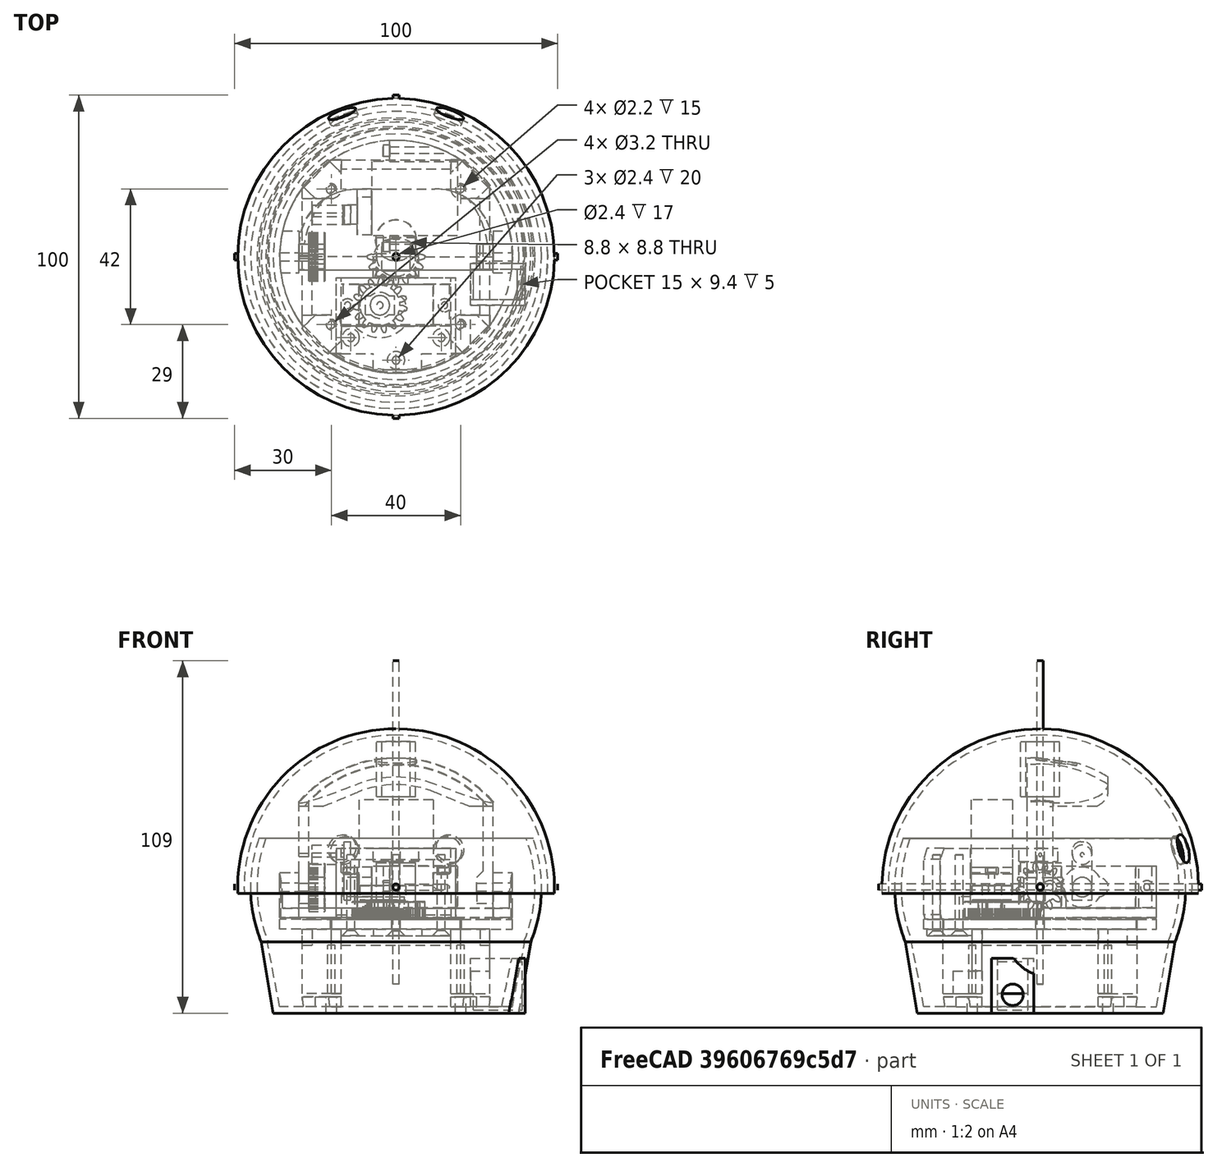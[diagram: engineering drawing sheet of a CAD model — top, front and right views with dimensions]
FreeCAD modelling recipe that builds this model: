
FCSTD DOCUMENT  (FreeCAD 0.18R16146 (Git))
Label: 2AxisDrive
License: All rights reserved
LicenseURL: http://en.wikipedia.org/wiki/All_rights_reserved
objects: Part::Cylinder×41, Part::Box×40, Part::Cut×20, Part::MultiFuse×20, Part::Chamfer×17, Part::Fillet×15, Part::Sphere×7, Part::Feature×4, Part::FeaturePython×3, Part::MultiCommon×3, Part::Cone×2
note: 172 computed .brp shape members not serialized (recipe doc carries the construction recipe); baked Part::Feature solids carry a one-line shape summary decoded from their .brp

FEATURE [Part::Cylinder] Cylinder001  label="Axis_Z"
  Angle = 360
  AttacherType = Attacher::AttachEngine3D
  Height = 100
  Placement = pos=(0,0,-30) rot=(0,0,1;0rad)
  Radius = 1
FEATURE [Part::Cylinder] Cylinder002  label="Axis_Y"
  Angle = 360
  AttacherType = Attacher::AttachEngine3D
  Height = 100
  Placement = pos=(0,50,0) rot=(1,0,0;1.5708rad)
  Radius = 1
FEATURE [Part::Cylinder] Cylinder003  label="Axis_X"
  Angle = 360
  AttacherType = Attacher::AttachEngine3D
  Height = 100
  Placement = pos=(-50,0,0) rot=(0,1,0;1.5708rad)
  Radius = 1
FEATURE [Part::Feature] Fusion001003001001006003002002001  label="Servo_1"
  Placement = pos=(-5,-15,3) rot=(0,0,1;1.5708rad)
  shape: bbox 33 x 12.8 x 35.5 mm, 23 faces (baked)
FEATURE [Part::Cone] Cone
  Angle = 360
  AttacherType = Attacher::AttachEngine3D
  Height = 21
  Placement = pos=(0,0,-37) rot=(0,0,1;0rad)
  Radius1 = 36
  Radius2 = 40
FEATURE [Part::Cone] Cone001
  Angle = 360
  AttacherType = Attacher::AttachEngine3D
  Height = 22.1
  Placement = pos=(0,0,-39) rot=(0,0,1;0rad)
  Radius1 = 38
  Radius2 = 41.7
FEATURE [Part::Sphere] Sphere001
  Angle1 = -90
  Angle2 = 90
  Angle3 = 360
  AttacherType = Attacher::AttachEngine3D
  Radius = 43
FEATURE [Part::Sphere] Sphere002
  Angle1 = -90
  Angle2 = 90
  Angle3 = 360
  AttacherType = Attacher::AttachEngine3D
  Radius = 45
FEATURE [Part::Box] Box027  label="Limit002"
  AttacherType = Attacher::AttachEngine3D
  Height = 50
  Length = 120
  Placement = pos=(-60,-60,15) rot=(0,0,1;0rad)
  Width = 120
FEATURE [Part::Cut] Cut007
  Base = -> Sphere002
  Tool = -> Sphere001
FEATURE [Part::Box] Box028  label="Limit003"
  AttacherType = Attacher::AttachEngine3D
  Height = 50
  Length = 120
  Placement = pos=(-60,-60,-67) rot=(0,0,1;0rad)
  Width = 120
FEATURE [Part::MultiFuse] Fusion001003001001006003002002007  label="BoxLimiters"
  Shapes = -> [Box028,Box027]
FEATURE [Part::Cut] Cut008  label="BoxRadius"
  Base = -> Cut007
  Tool = -> Fusion001003001001006003002002007
FEATURE [Part::Sphere] Sphere003
  Angle1 = -90
  Angle2 = 90
  Angle3 = 360
  AttacherType = Attacher::AttachEngine3D
  Radius = 49
FEATURE [Part::Sphere] Sphere004
  Angle1 = -90
  Angle2 = 90
  Angle3 = 360
  AttacherType = Attacher::AttachEngine3D
  Radius = 47
FEATURE [Part::Box] Box029  label="Limit004"
  AttacherType = Attacher::AttachEngine3D
  Height = 65
  Length = 120
  Placement = pos=(-60,-60,-67) rot=(0,0,1;0rad)
  Width = 120
FEATURE [Part::Cut] Cut010
  Base = -> Sphere003
  Tool = -> Sphere004
FEATURE [Part::Cut] Cut011  label="BoxTop"
  Base = -> Cut010
  Tool = -> Box029
FEATURE [Part::Box] Box030  label="Cube023"
  AttacherType = Attacher::AttachEngine3D
  Height = 17
  Length = 12
  Placement = pos=(-6,-6,28) rot=(0,0,1;0rad)
  Width = 12
FEATURE [Part::Box] Box031  label="Cube024"
  AttacherType = Attacher::AttachEngine3D
  Height = 20
  Length = 8.8
  Placement = pos=(-4.4,-4.4,28) rot=(0,0,1;0rad)
  Width = 8.8
FEATURE [Part::Cut] Cut012
  Base = -> Box030
  Tool = -> Box031
FEATURE [Part::MultiFuse] Fusion001003001001006003002002009  label="BoxCover"
  Shapes = -> [Cut012,Cut011]
FEATURE [Part::Feature] Fusion001003001001006003002002015001  label="EyeHolles"
  Placement = pos=(0,0,0) rot=(1,0,0;0.261799rad)
  shape: bbox 49.5 x 58.24 x 23.32 mm, 6 faces (baked)
FEATURE [Part::Feature] Fusion001003001001006003002002015002001  label="Fusion001003001001006003002002015003"
  Placement = pos=(0,0,0) rot=(1,0,0;0.261799rad)
  shape: bbox 40.43 x 44.55 x 21.37 mm, 6 faces (baked)
FEATURE [Part::MultiFuse] Fusion001003001001006003002002015002002
  Shapes = -> [Fusion001003001001006003002002015002001,Fusion001003001001006003002002015001]
FEATURE [Part::Cut] Cut019  label="Cover"
  Base = -> Fusion001003001001006003002002009
  Tool = -> Fusion001003001001006003002002015002002
FEATURE [Part::Cylinder] Cylinder005  label="RotaryBase"
  Angle = 180
  AttacherType = Attacher::AttachEngine3D
  Height = 3
  Placement = pos=(0,0,-9.5) rot=(0,0,-1;0rad)
  Radius = 36
FEATURE [Part::Cylinder] Cylinder008  label="Limit"
  Angle = 360
  AttacherType = Attacher::AttachEngine3D
  Height = 75
  Placement = pos=(0,0,-50) rot=(0,0,1;0rad)
  Radius = 45
FEATURE [Part::Box] Box040  label="Cube033"
  AttacherType = Attacher::AttachEngine3D
  Height = 10
  Length = 5
  Placement = pos=(25,-4,-5) rot=(0,0,1;0rad)
  Width = 8
FEATURE [Part::Box] Box041  label="Cube034"
  AttacherType = Attacher::AttachEngine3D
  Height = 10
  Length = 5
  Placement = pos=(-30,-4,-5) rot=(0,0,1;0rad)
  Width = 8
FEATURE [Part::Fillet] Fillet005
  Base = -> Box041
  Edges = 2 edges r=3.5: [Edge9,Edge11]
FEATURE [Part::Feature] Fusion001003001001006003002002015002003002  label="Servo_2"
  Placement = pos=(-5,13,0) rot=(1,0,0;3.14159rad)
  shape: bbox 35.5 x 33 x 12.8 mm, 23 faces (baked)
FEATURE [Part::Box] Box044  label="Cube037"
  AttacherType = Attacher::AttachEngine3D
  Height = 14
  Length = 6
  Placement = pos=(-36,-5,-9.5) rot=(0,0,1;0rad)
  Width = 13
FEATURE [Part::Box] Box045  label="Cube038"
  AttacherType = Attacher::AttachEngine3D
  Height = 14
  Length = 6
  Placement = pos=(30,-5,-9.5) rot=(0,0,1;0rad)
  Width = 13
FEATURE [Part::FeaturePython] involutegear  # WARN: FeaturePython — macro-defined, semantics opaque (R4)
  Placement = pos=(0,0,-9.5) rot=(0,0,1;0rad)
  backlash = 0
  beta = 0
  clearance = 0.25
  double_helix = false
  dw = 16
  head = 0
  height = 5
  module = 1
  numpoints = 6
  pressure_angle = 20
  properties_from_tool = false
  reversed_backlash = false
  shift = 0
  simple = false
  teeth = 16
  transverse_pitch = 3.14159
  undercut = false
  version = 0.0.3
FEATURE [Part::FeaturePython] involutegear001  label="Servo_1_gear_main"  # WARN: FeaturePython — macro-defined, semantics opaque (R4)
  Placement = pos=(-5,-15,-9.5) rot=(0,0,-1;0.139626rad)
  backlash = 0
  beta = 0
  clearance = 0.25
  double_helix = false
  dw = 15
  head = 0
  height = 5
  module = 1
  numpoints = 6
  pressure_angle = 20
  properties_from_tool = false
  reversed_backlash = false
  shift = 0
  simple = false
  teeth = 15
  transverse_pitch = 3.14159
  undercut = false
  version = 0.0.3
FEATURE [Part::Fillet] Fillet006
  Base = -> Box040
  Edges = 2 edges r=3.5: [Edge9,Edge11]
FEATURE [Part::Cylinder] Cylinder014  label="Axis_X005"
  Angle = 360
  AttacherType = Attacher::AttachEngine3D
  Height = 100
  Placement = pos=(-50,0,0) rot=(0,1,0;1.5708rad)
  Radius = 1.2
FEATURE [Part::Cylinder] Cylinder015  label="Axis_X006"
  Angle = 360
  AttacherType = Attacher::AttachEngine3D
  Height = 15
  Placement = pos=(-40,0,0) rot=(0,1,0;1.5708rad)
  Radius = 1.3
FEATURE [Part::Box] Box049  label="Cube042"
  AttacherType = Attacher::AttachEngine3D
  Height = 10
  Length = 30
  Placement = pos=(-15,1,-9.5) rot=(0,0,1;0rad)
  Width = 15
FEATURE [Part::Cut] Cut022011  label="Gear_2"
  Base = -> involutegear
  Tool = -> Box049
FEATURE [Part::Cylinder] Cylinder
  Angle = 180
  AttacherType = Attacher::AttachEngine3D
  Height = 17
  Placement = pos=(0,0,-9.5) rot=(0,0,1;3.14159rad)
  Radius = 6
FEATURE [Part::Box] Box053  label="Cube046"
  AttacherType = Attacher::AttachEngine3D
  Height = 16
  Length = 21
  Placement = pos=(-2,29.5,-9.5) rot=(0,0,1;0rad)
  Width = 8
FEATURE [Part::Cylinder] Cylinder020  label="Axis_X008"
  Angle = 360
  AttacherType = Attacher::AttachEngine3D
  Height = 25
  Placement = pos=(-5,33,0) rot=(0,1,0;1.5708rad)
  Radius = 1
FEATURE [Part::Cylinder] Cylinder021  label="Axis_X009"
  Angle = 360
  AttacherType = Attacher::AttachEngine3D
  Height = 25
  Placement = pos=(-10,3,0) rot=(0,1,0;1.5708rad)
  Radius = 1
FEATURE [Part::Box] Box056  label="Cube049"
  AttacherType = Attacher::AttachEngine3D
  Height = 18
  Length = 2
  Placement = pos=(-16,10,-4) rot=(-1,0,0;0rad)
  Width = 6
FEATURE [Part::Cylinder] Cylinder024  label="Axis_X010"
  Angle = 360
  AttacherType = Attacher::AttachEngine3D
  Height = 20
  Placement = pos=(-30,13,10) rot=(0,1,0;1.5708rad)
  Radius = 0.6
FEATURE [Part::Sphere] Sphere
  Angle1 = -90
  Angle2 = 90
  Angle3 = 360
  AttacherType = Attacher::AttachEngine3D
  Radius = 38
FEATURE [Part::Fillet] Fillet008  label="Servo_2_winch"
  Base = -> Box056
  Edges = 2 edges r=2.5: [Edge10,Edge12]
FEATURE [Part::Cylinder] Cylinder041  label="Cylinder024"
  Angle = 360
  AttacherType = Attacher::AttachEngine3D
  Height = 8
  Placement = pos=(-5,-15,-11) rot=(0,0,1;0rad)
  Radius = 10
FEATURE [Part::Box] Box077  label="Cube070"
  AttacherType = Attacher::AttachEngine3D
  Height = 38
  Length = 23
  Placement = pos=(-11.5,-21.5,-11) rot=(0,0,1;0rad)
  Width = 13
FEATURE [Part::Cylinder] Cylinder042  label="Base001"
  Angle = 360
  AttacherType = Attacher::AttachEngine3D
  Height = 3
  Placement = pos=(0,0,-13) rot=(0,0,1;0rad)
  Radius = 36
FEATURE [Part::Box] Box080  label="Cube073"
  AttacherType = Attacher::AttachEngine3D
  Height = 22
  Length = 37
  Placement = pos=(-18.5,-37.5,-10) rot=(0,0,1;0rad)
  Width = 31
FEATURE [Part::Sphere] Sphere005
  Angle1 = -90
  Angle2 = 90
  Angle3 = 360
  AttacherType = Attacher::AttachEngine3D
  Radius = 37
FEATURE [Part::Box] Box081  label="Cube074"
  AttacherType = Attacher::AttachEngine3D
  Height = 8
  Length = 34
  Placement = pos=(-17,-21.5,-10) rot=(0,0,1;0rad)
  Width = 16
FEATURE [Part::MultiFuse] Fusion001003001001006003002002015002003010016  label="ServoHollows"
  Shapes = -> [Box081,Box077,Cylinder041]
FEATURE [Part::Cylinder] Cylinder043  label="Base002"
  Angle = 360
  AttacherType = Attacher::AttachEngine3D
  Height = 50
  Placement = pos=(0,0,-14) rot=(0,0,1;0rad)
  Radius = 36
FEATURE [Part::Cylinder] Cylinder044  label="Axis_Z020"
  Angle = 360
  AttacherType = Attacher::AttachEngine3D
  Height = 25
  Placement = pos=(0,-32,-15) rot=(0,0,1;0rad)
  Radius = 1.2
FEATURE [Part::Cylinder] Cylinder045  label="Axis_Z021"
  Angle = 360
  AttacherType = Attacher::AttachEngine3D
  Height = 50
  Placement = pos=(-15,-15,-15) rot=(0,0,1;0rad)
  Radius = 1
FEATURE [Part::Cylinder] Cylinder046  label="Axis_Z022"
  Angle = 360
  AttacherType = Attacher::AttachEngine3D
  Height = 50
  Placement = pos=(15,-15,-15) rot=(0,0,1;0rad)
  Radius = 1
FEATURE [Part::Cylinder] Cylinder047  label="Axis_Z023"
  Angle = 360
  AttacherType = Attacher::AttachEngine3D
  Height = 25
  Placement = pos=(-14,-25,-15) rot=(0,0,1;0rad)
  Radius = 1.2
FEATURE [Part::Cylinder] Cylinder048  label="Axis_Z024"
  Angle = 360
  AttacherType = Attacher::AttachEngine3D
  Height = 25
  Placement = pos=(14,-25,-15) rot=(0,0,1;0rad)
  Radius = 1.2
FEATURE [Part::MultiFuse] Fusion001003001001006003002002015002003010017  label="ScrewHolles001"
  Shapes = -> [Cylinder044,Cylinder048,Cylinder045,Cylinder047,Cylinder046]
FEATURE [Part::Cylinder] Cylinder049  label="Axis_Z025"
  Angle = 360
  AttacherType = Attacher::AttachEngine3D
  Height = 100
  Placement = pos=(0,0,-30) rot=(0,0,1;0rad)
  Radius = 1.3
FEATURE [Part::Box] Box082  label="Cube075"
  AttacherType = Attacher::AttachEngine3D
  Height = 4
  Length = 14
  Placement = pos=(-7,-8.5,8) rot=(0,0,1;0rad)
  Width = 14
FEATURE [Part::MultiCommon] Common
  Shapes = -> [Cylinder043,Box080,Sphere005]
FEATURE [Part::Sphere] Sphere006
  Angle1 = -90
  Angle2 = 90
  Angle3 = 360
  AttacherType = Attacher::AttachEngine3D
  Radius = 40
FEATURE [Part::Cut] Cut022045
  Base = -> Sphere006
  Placement = pos=(0,0,0) rot=(0,-1,0;1.5708rad)
  Tool = -> Sphere
FEATURE [Part::Box] Box084  label="Cube077"
  AttacherType = Attacher::AttachEngine3D
  Height = 17
  Length = 8
  Placement = pos=(-2,0,-9.5) rot=(0,0,1;0rad)
  Width = 6.5
FEATURE [Part::Box] Box085  label="Cube078"
  AttacherType = Attacher::AttachEngine3D
  Height = 14
  Length = 8
  Placement = pos=(-6,0,-6.5) rot=(0,0,1;0rad)
  Width = 1
FEATURE [Part::Cylinder] Cylinder050  label="Limiter"
  Angle = 360
  AttacherType = Attacher::AttachEngine3D
  Height = 50
  Placement = pos=(0,0,-14) rot=(0,0,1;0rad)
  Radius = 36
FEATURE [Part::Cylinder] Cylinder052  label="Axis_Z027"
  Angle = 360
  AttacherType = Attacher::AttachEngine3D
  Height = 30
  Placement = pos=(0,0,-15) rot=(0,0,1;0rad)
  Radius = 1.2
FEATURE [Part::Box] Box086  label="Cube079"
  AttacherType = Attacher::AttachEngine3D
  Height = 25
  Length = 3
  Placement = pos=(-30,-4,2) rot=(0,0,1;0rad)
  Width = 8
FEATURE [Part::Box] Box087  label="Cube080"
  AttacherType = Attacher::AttachEngine3D
  Height = 25
  Length = 3
  Placement = pos=(27,-4,2) rot=(0,0,1;0rad)
  Width = 8
FEATURE [Part::Chamfer] Chamfer013
  Base = -> Box087
  Edges = 1 edges r=2: [Edge6]
FEATURE [Part::Chamfer] Chamfer014
  Base = -> Fillet006
  Edges = 1 edges r=2: [Edge3]
FEATURE [Part::Cut] Cut
  Base = -> Cut022045
  Tool = -> Cylinder008
FEATURE [Part::Box] Box088  label="Cube081"
  AttacherType = Attacher::AttachEngine3D
  Height = 31
  Length = 60
  Placement = pos=(-30,-4,24) rot=(0,0,1;0rad)
  Width = 25
FEATURE [Part::Fillet] Fillet  label="Hindge002"
  Base = -> Box044
  Edges = 1 edges r=8: [Edge12]
FEATURE [Part::Fillet] Fillet011  label="Hindge001"
  Base = -> Box045
  Edges = 1 edges r=8: [Edge12]
FEATURE [Part::Fillet] Fillet012
  Base = -> Box082
  Edges = 2 edges r=6: [Edge3,Edge7]
FEATURE [Part::Cut] Cut022059
  Base = -> Fillet012
  Tool = -> Cylinder049
FEATURE [Part::Chamfer] Chamfer019
  Base = -> Box086
  Edges = 1 edges r=2: [Edge2]
FEATURE [Part::Cylinder] Cylinder053  label="Axis_Z028"
  Angle = 360
  AttacherType = Attacher::AttachEngine3D
  Height = 25
  Placement = pos=(-14,-25,-25) rot=(0,0,1;0rad)
  Radius = 1.2
FEATURE [Part::Cylinder] Cylinder054  label="Axis_Z029"
  Angle = 360
  AttacherType = Attacher::AttachEngine3D
  Height = 25
  Placement = pos=(14,-25,-25) rot=(0,0,1;0rad)
  Radius = 1.2
FEATURE [Part::Cylinder] Cylinder055  label="Axis_Z030"
  Angle = 360
  AttacherType = Attacher::AttachEngine3D
  Height = 25
  Placement = pos=(0,-32,-25) rot=(0,0,1;0rad)
  Radius = 1.2
FEATURE [Part::Cylinder] Cylinder056  label="Axis_Z031"
  Angle = 360
  AttacherType = Attacher::AttachEngine3D
  Height = 25
  Placement = pos=(0,0,-30) rot=(0,0,1;0rad)
  Radius = 1.3
FEATURE [Part::Fillet] Fillet014
  Base = -> Box088
  Edges = 2 edges r=18: [Edge3,Edge7]
FEATURE [Part::Cylinder] Cylinder057  label="Axis_X011"
  Angle = 360
  AttacherType = Attacher::AttachEngine3D
  Height = 10
  Placement = pos=(-26,13,10) rot=(0,1,0;1.5708rad)
  Radius = 3
FEATURE [Part::Cylinder] Cylinder058  label="Axis_X012"
  Angle = 360
  AttacherType = Attacher::AttachEngine3D
  Height = 15
  Placement = pos=(25,0,0) rot=(0,1,0;1.5708rad)
  Radius = 1.3
FEATURE [Part::MultiFuse] Fusion001003001001006003002002015002003010040  label="ServoHolderHolles"
  Shapes = -> [Cylinder021,Cylinder020,Cylinder052,Cylinder015,Cylinder058]
FEATURE [Part::MultiFuse] Fusion001003001001006003002002015002003010041  label="Axis"
  Shapes = -> [Box085,Cylinder,Cut022011,Box084]
FEATURE [Part::MultiFuse] Fusion001003001001006003002002015002003010042  label="HolderBody"
  Shapes = -> [Fusion001003001001006003002002015002003010041,Box053,Fillet,Fillet011,Cylinder005]
FEATURE [Part::MultiCommon] Common005
  Shapes = -> [Fusion001003001001006003002002015002003010042,Cylinder050]
FEATURE [Part::Cut] Cut022065  label="Servo_2_holder"
  Base = -> Common005
  Tool = -> Fusion001003001001006003002002015002003010040
FEATURE [Part::MultiCommon] Common006
  Shapes = -> [Cut,Fillet014]
FEATURE [Part::Cylinder] Cylinder059  label="Axis_X013"
  Angle = 360
  AttacherType = Attacher::AttachEngine3D
  Height = 15
  Placement = pos=(-35,0,10) rot=(0,1,0;1.5708rad)
  Radius = 0.5
FEATURE [Part::Chamfer] Chamfer
  Base = -> Fillet005
  Edges = 1 edges r=2: [Edge13]
FEATURE [Part::MultiFuse] Fusion  label="ArchBody"
  Shapes = -> [Common006,Chamfer019,Chamfer013,Chamfer014,Chamfer]
FEATURE [Part::Cut] Cut022067  label="WinchAdapter"
  Base = -> Cylinder057
  Tool = -> Cylinder024
FEATURE [Part::FeaturePython] involutegear002  # WARN: FeaturePython — macro-defined, semantics opaque (R4)
  Placement = pos=(-27,0,0) rot=(0,1,0;1.5708rad)
  backlash = 0
  beta = 0
  clearance = 0.25
  double_helix = false
  dw = 13
  head = 0
  height = 5
  module = 1
  numpoints = 6
  pressure_angle = 20
  properties_from_tool = false
  reversed_backlash = false
  shift = 0
  simple = false
  teeth = 13
  transverse_pitch = 3.14159
  undercut = false
  version = 0.0.3
FEATURE [Part::Cylinder] Cylinder060  label="Cylinder025"
  Angle = 360
  AttacherType = Attacher::AttachEngine3D
  Height = 4
  Placement = pos=(-5,-15,-8.5) rot=(0,0,1;0rad)
  Radius = 4
FEATURE [Part::Cylinder] Cylinder061  label="Cylinder026"
  Angle = 360
  AttacherType = Attacher::AttachEngine3D
  Height = 10
  Placement = pos=(-5,-15,-9.5) rot=(0,0,1;0rad)
  Radius = 1
FEATURE [Part::MultiFuse] Fusion001003001001006003002002015002003010044  label="Servo1_GearHolle"
  Shapes = -> [Cylinder061,Cylinder060]
FEATURE [Part::Cut] Cut022068
  Base = -> involutegear001
  Tool = -> Fusion001003001001006003002002015002003010044
FEATURE [Part::Box] Box  label="Cube"
  AttacherType = Attacher::AttachEngine3D
  Height = 4
  Length = 9
  Placement = pos=(-9.5,-17.9,-8.5) rot=(0,0,1;0rad)
  Width = 5.8
FEATURE [Part::Cut] Cut022069  label="Servo_1_gear"
  Base = -> Cut022068
  Tool = -> Box
FEATURE [Part::Box] Box089  label="Cube082"
  AttacherType = Attacher::AttachEngine3D
  Height = 23
  Length = 12
  Placement = pos=(17,18,-33) rot=(0,0,1;0rad)
  Width = 12
FEATURE [Part::Cylinder] Cylinder062  label="Screw001"
  Angle = 360
  AttacherType = Attacher::AttachEngine3D
  Height = 15
  Placement = pos=(20,21,-33) rot=(0,0,1;0rad)
  Radius = 1.1
FEATURE [Part::Cylinder] Cylinder063  label="Screw002"
  Angle = 360
  AttacherType = Attacher::AttachEngine3D
  Height = 15
  Placement = pos=(-20,21,-33) rot=(0,0,1;0rad)
  Radius = 1.1
FEATURE [Part::Cylinder] Cylinder064  label="Screw003"
  Angle = 360
  AttacherType = Attacher::AttachEngine3D
  Height = 15
  Placement = pos=(-20,-21,-33) rot=(0,0,1;0rad)
  Radius = 1.1
FEATURE [Part::Cylinder] Cylinder065  label="Screw004"
  Angle = 360
  AttacherType = Attacher::AttachEngine3D
  Height = 15
  Placement = pos=(20,-21,-33) rot=(0,0,1;0rad)
  Radius = 1.1
FEATURE [Part::Fillet] Fillet015
  Base = -> Box089
  Edges = 1 edges r=3: [Edge1]
FEATURE [Part::Chamfer] Chamfer020
  Base = -> Fillet015
  Edges = 1 edges r=9: [Edge12]
FEATURE [Part::Box] Box090  label="Cube083"
  AttacherType = Attacher::AttachEngine3D
  Height = 23
  Length = 12
  Placement = pos=(-29,18,-33) rot=(0,0,1;0rad)
  Width = 12
FEATURE [Part::Fillet] Fillet016
  Base = -> Box090
  Edges = 1 edges r=3: [Edge5]
FEATURE [Part::Chamfer] Chamfer021
  Base = -> Fillet016
  Edges = 1 edges r=9: [Edge12]
FEATURE [Part::Box] Box091  label="Cube084"
  AttacherType = Attacher::AttachEngine3D
  Height = 23
  Length = 12
  Placement = pos=(-29,-30,-33) rot=(0,0,1;0rad)
  Width = 12
FEATURE [Part::Fillet] Fillet017
  Base = -> Box091
  Edges = 1 edges r=3: [Edge7]
FEATURE [Part::Chamfer] Chamfer022
  Base = -> Fillet017
  Edges = 1 edges r=9: [Edge12]
FEATURE [Part::Box] Box092  label="Cube085"
  AttacherType = Attacher::AttachEngine3D
  Height = 23
  Length = 12
  Placement = pos=(17,-30,-33) rot=(0,0,1;0rad)
  Width = 12
FEATURE [Part::Fillet] Fillet018
  Base = -> Box092
  Edges = 1 edges r=3: [Edge3]
FEATURE [Part::Chamfer] Chamfer023
  Base = -> Fillet018
  Edges = 1 edges r=9: [Edge12]
FEATURE [Part::Box] Box093  label="Cube086"
  AttacherType = Attacher::AttachEngine3D
  Height = 8
  Length = 3
  Placement = pos=(26,-20,-18) rot=(0,0,1;0rad)
  Width = 40
FEATURE [Part::Box] Box094  label="Cube087"
  AttacherType = Attacher::AttachEngine3D
  Height = 8
  Length = 3
  Placement = pos=(-29,-20,-18) rot=(0,0,1;0rad)
  Width = 40
FEATURE [Part::Box] Box095  label="Cube088"
  AttacherType = Attacher::AttachEngine3D
  Height = 5
  Length = 40
  Placement = pos=(-20,-30,-15) rot=(0,0,1;0rad)
  Width = 9
FEATURE [Part::Box] Box096  label="Cube089"
  AttacherType = Attacher::AttachEngine3D
  Height = 8
  Length = 40
  Placement = pos=(-20,27,-18) rot=(0,0,1;0rad)
  Width = 3
FEATURE [Part::Box] Box098  label="Cube091"
  AttacherType = Attacher::AttachEngine3D
  Height = 17
  Length = 34
  Placement = pos=(-17,-21.5,4.5) rot=(0,0,1;0rad)
  Width = 13
FEATURE [Part::MultiFuse] Fusion001003001001006003002002015002003010047  label="HolderHolles"
  Shapes = -> [Box098,Fusion001003001001006003002002015002003010016,Fusion001003001001006003002002015002003010017]
FEATURE [Part::MultiFuse] Fusion001003001001006003002002015002003010048  label="HolderBody001"
  Shapes = -> [Cut022059,Common]
FEATURE [Part::Cut] Cut022071  label="Servo_1_holder"
  Base = -> Fusion001003001001006003002002015002003010048
  Tool = -> Fusion001003001001006003002002015002003010047
FEATURE [Part::Box] Box099  label="Cube092"
  AttacherType = Attacher::AttachEngine3D
  Height = 5
  Length = 15
  Placement = pos=(-7,-35,-15) rot=(0,0,1;0rad)
  Width = 9
FEATURE [Part::MultiFuse] Fusion001003001001006003002002015002003010049  label="BasePannelBody"
  Shapes = -> [Cylinder042,Chamfer023,Chamfer020,Chamfer021,Chamfer022,Box093,Box094,Box095,Box096,Box099]
FEATURE [Part::MultiFuse] Fusion001003001001006003002002015002003010050  label="BaseHolles"
  Shapes = -> [Cylinder056,Cylinder053,Cylinder054,Cylinder055,Cylinder062,Cylinder063,Cylinder064,Cylinder065]
FEATURE [Part::Cut] Cut022072
  Base = -> Fusion001003001001006003002002015002003010049
  Tool = -> Fusion001003001001006003002002015002003010050
FEATURE [Part::Chamfer] Chamfer024  label="BasePannel001"
  Base = -> Cut022072
  Edges = 3 edges r=1.5: [Edge156,Edge157,Edge241]
FEATURE [Part::Cylinder] Cylinder066  label="Magnet"
  Angle = 360
  AttacherType = Attacher::AttachEngine3D
  Height = 2
  Placement = pos=(0,5,38.5) rot=(-1,0,0;0.139626rad)
  Radius = 6.4
FEATURE [Part::MultiFuse] Fusion001003001001006003002002015002003010051  label="ArchHollows"
  Shapes = -> [Cylinder066,Cylinder014,Cylinder059]
FEATURE [Part::Cut] Cut022073  label="TiltArch"
  Base = -> Fusion
  Tool = -> Fusion001003001001006003002002015002003010051
FEATURE [Part::Cylinder] Cylinder067  label="Screw005"
  Angle = 360
  AttacherType = Attacher::AttachEngine3D
  Height = 15
  Placement = pos=(20,-21,-40) rot=(0,0,1;0rad)
  Radius = 1.6
FEATURE [Part::Cylinder] Cylinder068  label="Screw006"
  Angle = 360
  AttacherType = Attacher::AttachEngine3D
  Height = 15
  Placement = pos=(20,21,-40) rot=(0,0,1;0rad)
  Radius = 1.6
FEATURE [Part::Cylinder] Cylinder069  label="Screw007"
  Angle = 360
  AttacherType = Attacher::AttachEngine3D
  Height = 15
  Placement = pos=(-20,21,-40) rot=(0,0,1;0rad)
  Radius = 1.6
FEATURE [Part::Cylinder] Cylinder070  label="Screw008"
  Angle = 360
  AttacherType = Attacher::AttachEngine3D
  Height = 15
  Placement = pos=(-20,-21,-40) rot=(0,0,1;0rad)
  Radius = 1.6
FEATURE [Part::Box] Box100  label="Cube093"
  AttacherType = Attacher::AttachEngine3D
  Height = 5
  Length = 12
  Placement = pos=(17,18,-39) rot=(0,0,1;0rad)
  Width = 12
FEATURE [Part::Fillet] Fillet019
  Base = -> Box100
  Edges = 1 edges r=3: [Edge1]
FEATURE [Part::Chamfer] Chamfer026
  Base = -> Fillet019
  Edges = 1 edges r=6: [Edge12]
FEATURE [Part::Box] Box101  label="Cube094"
  AttacherType = Attacher::AttachEngine3D
  Height = 5
  Length = 12
  Placement = pos=(-29,18,-39) rot=(0,0,1;0rad)
  Width = 12
FEATURE [Part::Fillet] Fillet020
  Base = -> Box101
  Edges = 1 edges r=3: [Edge5]
FEATURE [Part::Chamfer] Chamfer027
  Base = -> Fillet020
  Edges = 1 edges r=6: [Edge12]
FEATURE [Part::Box] Box102  label="Cube095"
  AttacherType = Attacher::AttachEngine3D
  Height = 5
  Length = 12
  Placement = pos=(-29,-30,-39) rot=(0,0,1;0rad)
  Width = 12
FEATURE [Part::Fillet] Fillet021
  Base = -> Box102
  Edges = 1 edges r=3: [Edge7]
FEATURE [Part::Chamfer] Chamfer028
  Base = -> Fillet021
  Edges = 1 edges r=6: [Edge12]
FEATURE [Part::Box] Box103  label="Cube096"
  AttacherType = Attacher::AttachEngine3D
  Height = 5
  Length = 12
  Placement = pos=(17,-30,-39) rot=(0,0,1;0rad)
  Width = 12
FEATURE [Part::Fillet] Fillet022
  Base = -> Box103
  Edges = 1 edges r=3: [Edge3]
FEATURE [Part::Chamfer] Chamfer025
  Base = -> Fillet022
  Edges = 1 edges r=6: [Edge12]
FEATURE [Part::Chamfer] Chamfer029  label="PCBHolder004"
  Base = -> Chamfer026
  Edges = 2 edges r=4: [Edge9,Edge14]
FEATURE [Part::Chamfer] Chamfer030  label="PCBHolder001"
  Base = -> Chamfer025
  Edges = 2 edges r=4: [Edge9,Edge14]
FEATURE [Part::Chamfer] Chamfer031  label="PCBHolder002"
  Base = -> Chamfer027
  Edges = 2 edges r=4: [Edge9,Edge14]
FEATURE [Part::Chamfer] Chamfer032  label="PCBHolder003"
  Base = -> Chamfer028
  Edges = 2 edges r=4: [Edge8,Edge15]
FEATURE [Part::Cut] Cut022074  label="ConeBody"
  Base = -> Cone001
  Tool = -> Cone
FEATURE [Part::MultiFuse] Fusion001003001001006003002002015002003010056  label="BoxScrews"
  Shapes = -> [Cylinder070,Cylinder067,Cylinder069,Cylinder068]
FEATURE [Part::Box] Box104  label="ConnectorSpace"
  AttacherType = Attacher::AttachEngine3D
  Height = 17
  Length = 17
  Placement = pos=(23,-15,-39) rot=(0,0,1;0rad)
  Width = 13
FEATURE [Part::MultiFuse] Fusion001003001001006003002002015002003010057  label="BoxBottom"
  Shapes = -> [Chamfer029,Chamfer030,Cut022074,Chamfer031,Chamfer032,Box104]
FEATURE [Part::Box] Box105  label="ConnectorHolle"
  AttacherType = Attacher::AttachEngine3D
  Height = 15
  Length = 15
  Placement = pos=(24,-13.2,-38) rot=(0,0,1;0rad)
  Width = 9.4
FEATURE [Part::Box] Box106  label="ConnectorHolle001"
  AttacherType = Attacher::AttachEngine3D
  Height = 11
  Length = 15
  Placement = pos=(22.5,-13.2,-33) rot=(0,0,1;0rad)
  Width = 9.4
FEATURE [Part::Cylinder] Cylinder071  label="Cylinder027"
  Angle = 360
  AttacherType = Attacher::AttachEngine3D
  Height = 20
  Placement = pos=(26,-8.5,-33.3) rot=(0,1,0;1.5708rad)
  Radius = 3.3
FEATURE [Part::MultiFuse] Fusion001003001001006003002002015002003010058  label="ConnectorHolles"
  Shapes = -> [Cylinder071,Box105,Box106]
FEATURE [Part::MultiFuse] Fusion001003001001006003002002015002003010059  label="BoxHolles"
  Shapes = -> [Fusion001003001001006003002002015002003010056,Fusion001003001001006003002002015002003010058]
FEATURE [Part::Cut] Cut022075
  Base = -> Fusion001003001001006003002002015002003010057
  Tool = -> Fusion001003001001006003002002015002003010059
FEATURE [Part::MultiFuse] Fusion001003001001006003002002015002003010060  label="BottomBox"
  Shapes = -> [Cut008,Cut022075]
FEATURE [Part::Box] Box107  label="ConnectorSpace001"
  AttacherType = Attacher::AttachEngine3D
  Height = 9
  Length = 17
  Placement = pos=(23,-30,-35) rot=(0,0,1;0rad)
  Width = 13
FEATURE [Part::Cut] Cut022076  label="BasePannel"
  Base = -> Chamfer024
  Tool = -> Box107
